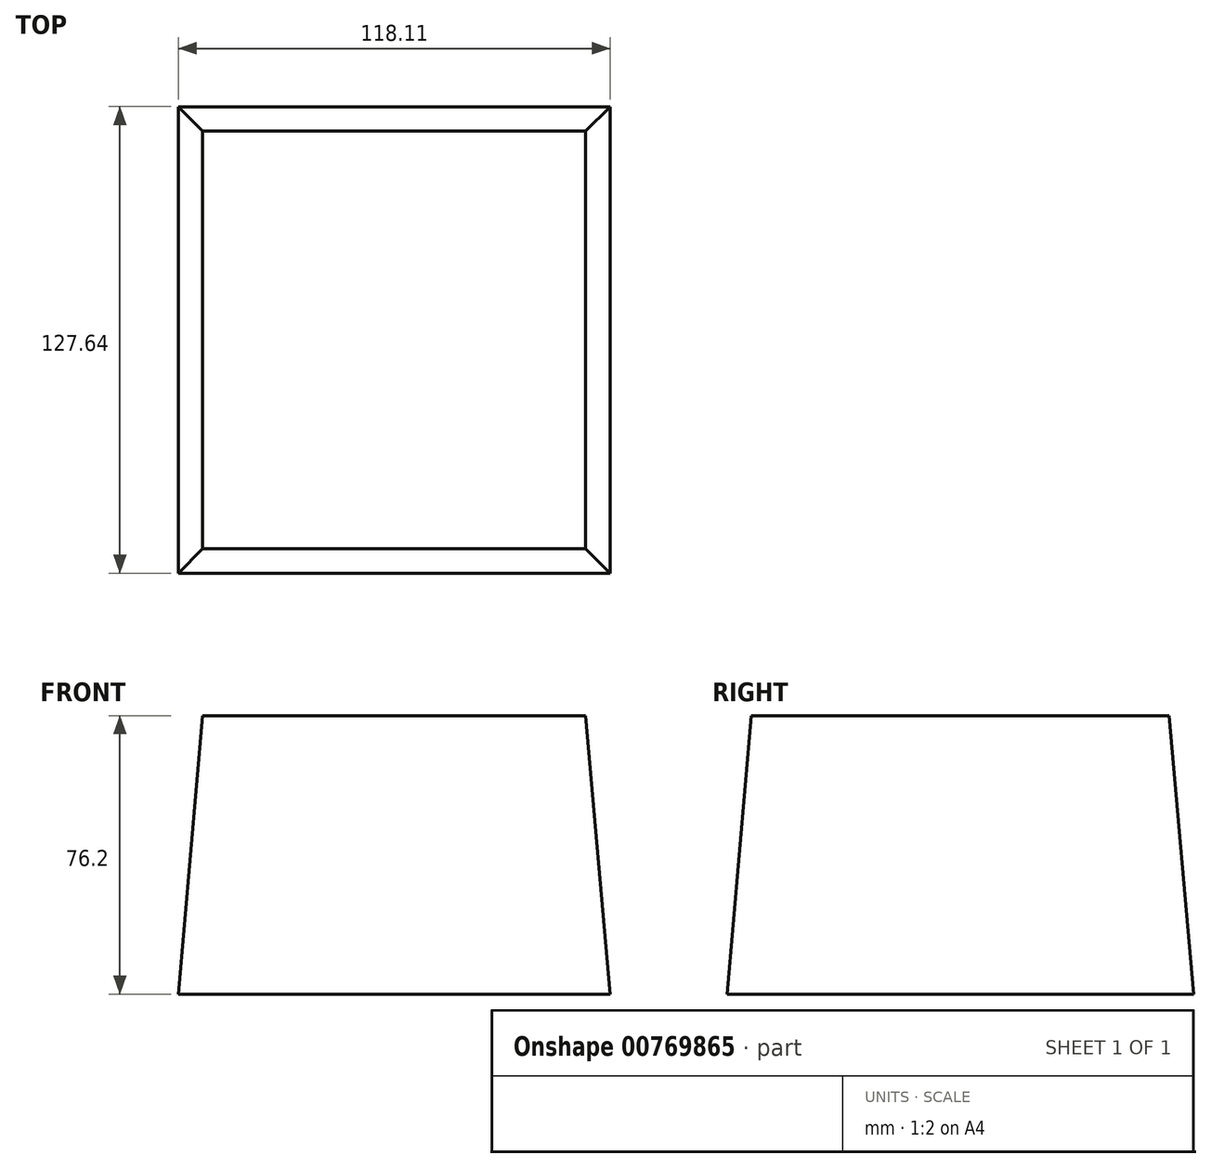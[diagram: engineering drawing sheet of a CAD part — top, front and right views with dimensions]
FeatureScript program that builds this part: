
annotation { "Feature Type Name" : "Feature", "Feature Type Description" : "" }
export const myFeature = defineFeature(function(context is Context, id is Id, definition is map)
    precondition{}
    {
        {
            var Q0;
            Q0=qCreatedBy(makeId("Top.planeOp"),FACE);
            var sketch = newSketch(context, id + "F0", { "sketchPlane" : qUnion([Q0])});
            skLineSegment(sketch, "E0.bottom", {"start": v(-35.67, 70.09) * mm, "end": v(69.1, 70.09) * mm});
            skLineSegment(sketch, "E0.top", {"start": v(-35.67, -44.21) * mm, "end": v(69.1, -44.21) * mm});
            skLineSegment(sketch, "E0.left", {"start": v(-35.67, 70.09) * mm, "end": v(-35.67, -44.21) * mm});
            skLineSegment(sketch, "E0.right", {"start": v(69.1, 70.09) * mm, "end": v(69.1, -44.21) * mm});
            skSolve(sketch);
        }
        {
            var Q0;
            Q0 = qSketchRegion(id + "F0", true);
            extrude(context, id + "F1", {"entities" : qUnion([Q0]), "oppositeDirection" : true, "depth" : 76.2 * mm, "offsetDistance" : 25.4 * mm, "hasDraft" : true, "draftAngle" : 5 * degree});
        }
    });
